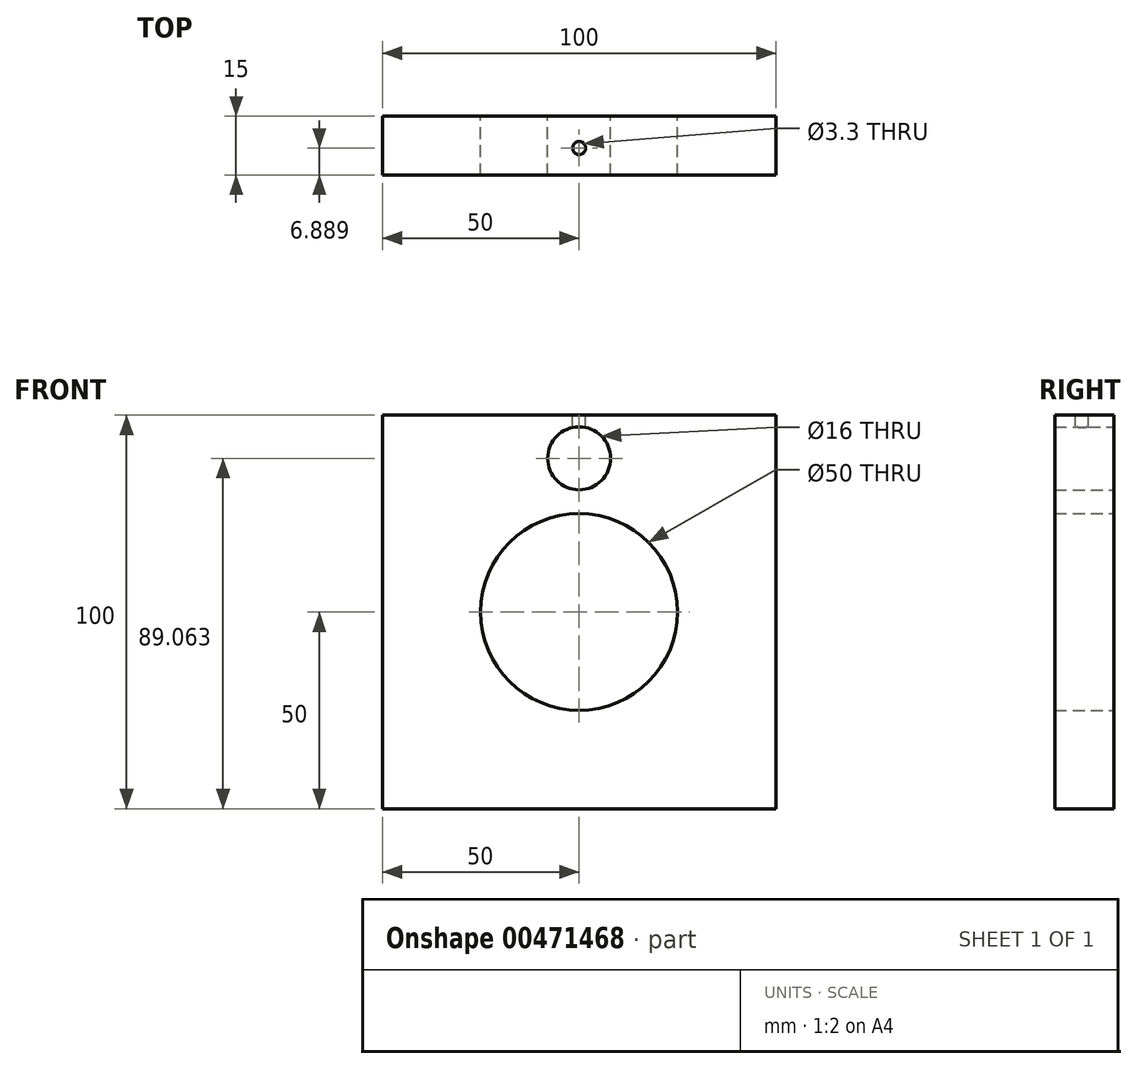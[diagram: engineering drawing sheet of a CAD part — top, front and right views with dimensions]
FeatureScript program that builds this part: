
annotation { "Feature Type Name" : "Feature", "Feature Type Description" : "" }
export const myFeature = defineFeature(function(context is Context, id is Id, definition is map)
    precondition{}
    {
        {
            var Q0;
            Q0=qCreatedBy(makeId("Front.planeOp"),FACE);
            var sketch = newSketch(context, id + "F0", { "sketchPlane" : qUnion([Q0])});
            skLineSegment(sketch, "E0.bottom", {"start": v(-50, 50) * mm, "end": v(50, 50) * mm});
            skLineSegment(sketch, "E0.top", {"start": v(-50, -50) * mm, "end": v(50, -50) * mm});
            skLineSegment(sketch, "E0.left", {"start": v(-50, 50) * mm, "end": v(-50, -50) * mm});
            skLineSegment(sketch, "E0.right", {"start": v(50, 50) * mm, "end": v(50, -50) * mm});
            skSolve(sketch);
        }
        {
            var Q0;
            Q0=qCreatedBy(makeId("Front.planeOp"),FACE);
            var sketch = newSketch(context, id + "F1", { "sketchPlane" : qUnion([Q0])});
            skCircle(sketch, "E1", {"center": v(0, 0) * mm, "radius": 25 * mm});
            skSolve(sketch);
        }
        {
            var Q0;
            Q0=makeQuery(id+"F0.imprint","IMPRINT",FACE,{"disambiguationData":[TD([[makeQuery(id+"F0.imprint","IMPRINT",EDGE,{"derivedFrom":sQuery(id+"F0.wireOp",EDGE,"E0.bottom")}),-1.0]])]});
            extrude(context, id + "F2", {"entities" : qUnion([Q0]), "depth" : 15 * mm, "offsetDistance" : 25 * mm});
        }
        {
            var Q0;
            Q0 = qSketchRegion(id + "F1", true);
            extrude(context, id + "F3", {"entities" : qUnion([Q0]), "operationType" : NewBodyOperationType.REMOVE, "endBound" : BoundingType.THROUGH_ALL, "depth" : 25 * mm, "offsetDistance" : 25 * mm});
        }
        {
            var Q0;
            Q0=qCreatedBy(makeId("Front.planeOp"),FACE);
            var sketch = newSketch(context, id + "F4", { "sketchPlane" : qUnion([Q0])});
            skCircle(sketch, "E2", {"center": v(0, 39.06) * mm, "radius": 8 * mm});
            skSolve(sketch);
        }
        {
            var Q0;
            Q0 = qSketchRegion(id + "F4", true);
            extrude(context, id + "F5", {"entities" : qUnion([Q0]), "operationType" : NewBodyOperationType.REMOVE, "endBound" : BoundingType.THROUGH_ALL, "depth" : 25 * mm, "offsetDistance" : 25 * mm});
        }
        {
            var Q0;
            Q0=makeQuery(id+"F2.opExtrude","SWEPT_FACE",FACE,{"disambiguationData":[OSD([sQuery(id+"F0.wireOp",EDGE,"E0.bottom")])]});
            var sketch = newSketch(context, id + "F6", { "sketchPlane" : qUnion([Q0])});
            skPoint(sketch, "E3", {"position": v(0, -8.11) * mm});
            skSolve(sketch);
        }
        {
            var Q0;
            Q0=sQuery(id+"F6.wireOp",VERTEX,"E3");
            var Q1;
            Q1=makeQuery(id+"F2.opExtrude","SWEPT_BODY",BODY,{"disambiguationData":[OSD([sQuery(id+"F0.wireOp",EDGE,"E0.bottom"),sQuery(id+"F0.wireOp",EDGE,"E0.top"),sQuery(id+"F0.wireOp",EDGE,"E0.left"),sQuery(id+"F0.wireOp",EDGE,"E0.right")])]});
            hole(context, id + "F7", {"style" : HoleStyle.SIMPLE, "endStyle" : HoleEndStyle.BLIND, "standardTappedOrClearance" : lookupTablePath({ "standard" : "ISO", "fit" : "Normal", "size" : "M3", "type" : "Clearance" }), "standardBlindInLast" : lookupTablePath({ "fit" : "Standard", "standard" : "ISO", "size" : "M3", "type" : "Clearance" }), "holeDiameter" : 3.3 * mm, "holeDepth" : 13.5 * mm, "isTappedThrough" : true, "tappedDepth" : 12 * mm, "tapClearance" : 3, "locations" : qUnion([Q0]), "scope" : qUnion([Q1])});
        }
    });
